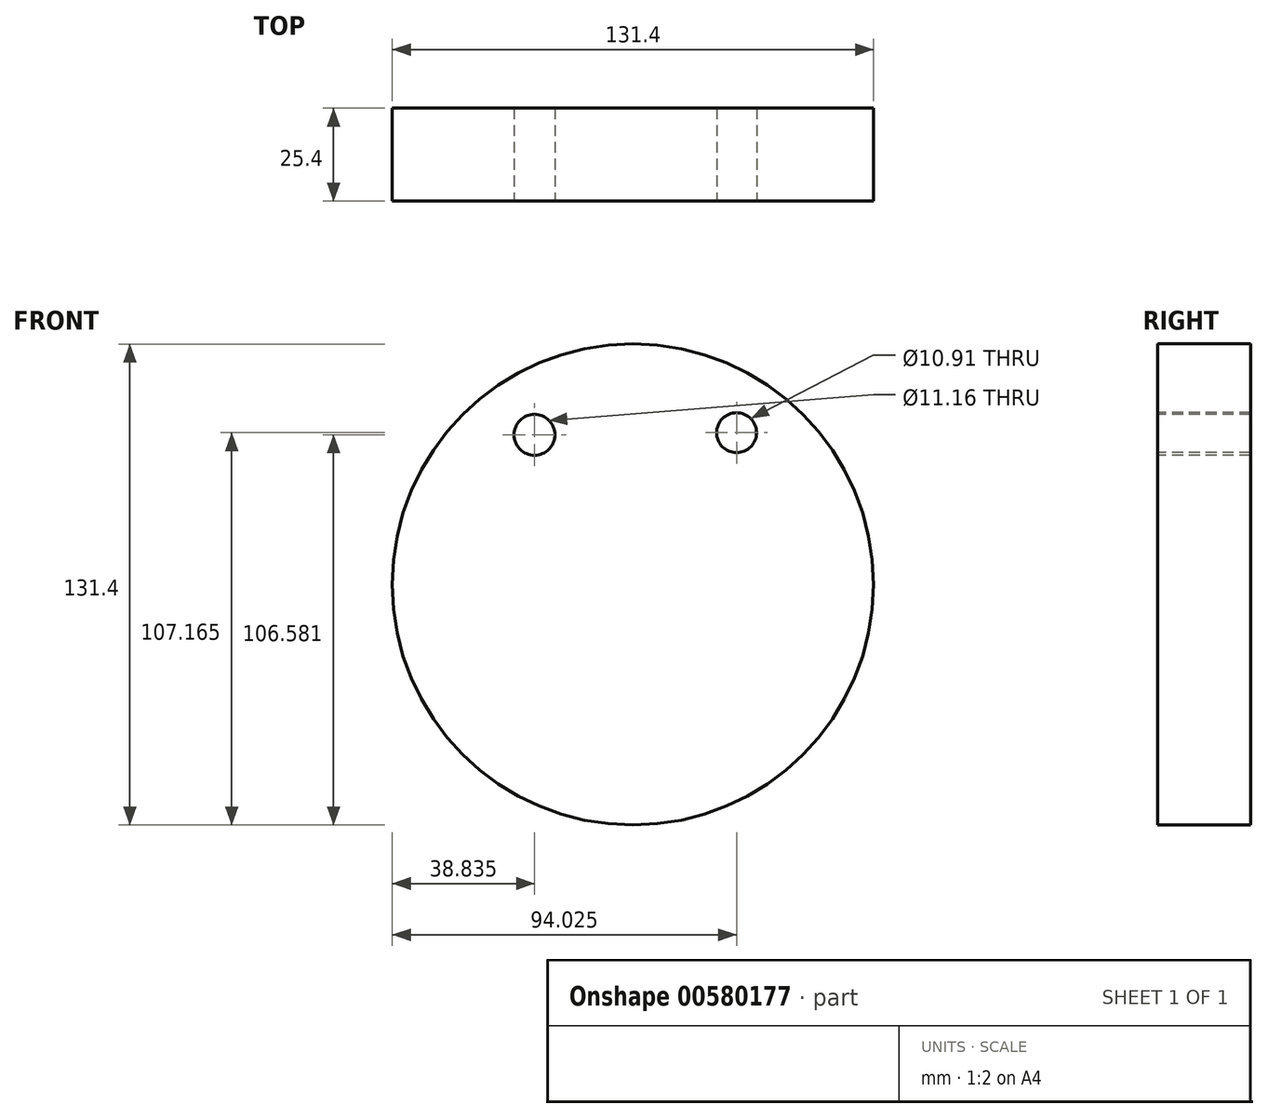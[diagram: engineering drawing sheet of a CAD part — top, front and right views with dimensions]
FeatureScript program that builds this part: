
annotation { "Feature Type Name" : "Feature", "Feature Type Description" : "" }
export const myFeature = defineFeature(function(context is Context, id is Id, definition is map)
    precondition{}
    {
        {
            var Q0;
            Q0=qCreatedBy(makeId("Front.planeOp"),FACE);
            var sketch = newSketch(context, id + "F0", { "sketchPlane" : qUnion([Q0])});
            skCircle(sketch, "E0", {"center": v(0, 0) * mm, "radius": 65.7 * mm});
            skSolve(sketch);
        }
        {
            var Q0;
            Q0=makeQuery(id+"F0.imprint","IMPRINT",FACE,{"disambiguationData":[TD([[makeQuery(id+"F0.imprint","IMPRINT",EDGE,{"derivedFrom":sQuery(id+"F0.wireOp",EDGE,"E0")}),1.0]])]});
            extrude(context, id + "F1", {"entities" : qUnion([Q0]), "depth" : 25.4 * mm, "offsetDistance" : 25.4 * mm});
        }
        {
            var Q0;
            Q0=makeQuery(id+"F1.opExtrude","CAP_FACE",FACE,{"disambiguationData":[OSD([sQuery(id+"F0.wireOp",EDGE,"E0")])],"isStart":false});
            var sketch = newSketch(context, id + "F2", { "sketchPlane" : qUnion([Q0])});
            skCircle(sketch, "E1", {"center": v(-26.86, 40.88) * mm, "radius": 5.58 * mm});
            skCircle(sketch, "E2", {"center": v(28.32, 41.47) * mm, "radius": 5.46 * mm});
            skSolve(sketch);
        }
        {
            var Q0;
            Q0=makeQuery(id+"F2.imprint","IMPRINT",FACE,{"disambiguationData":[TD([[makeQuery(id+"F2.imprint","IMPRINT",EDGE,{"derivedFrom":sQuery(id+"F2.wireOp",EDGE,"E1")}),1.0]])]});
            var Q1;
            Q1=makeQuery(id+"F2.imprint","IMPRINT",FACE,{"disambiguationData":[TD([[makeQuery(id+"F2.imprint","IMPRINT",EDGE,{"derivedFrom":sQuery(id+"F2.wireOp",EDGE,"E2")}),1.0]])]});
            var Q2;
            Q2=sQuery(id+"F2.wireOp",EDGE,"E1");
            var Q3;
            Q3=sQuery(id+"F2.wireOp",EDGE,"E2");
            extrude(context, id + "F3", {"entities" : qUnion([Q0, Q1]), "operationType" : NewBodyOperationType.REMOVE, "surfaceEntities" : qUnion([Q2, Q3]), "endBound" : BoundingType.THROUGH_ALL, "oppositeDirection" : true, "depth" : 25.4 * mm, "offsetDistance" : 25.4 * mm});
        }
    });
